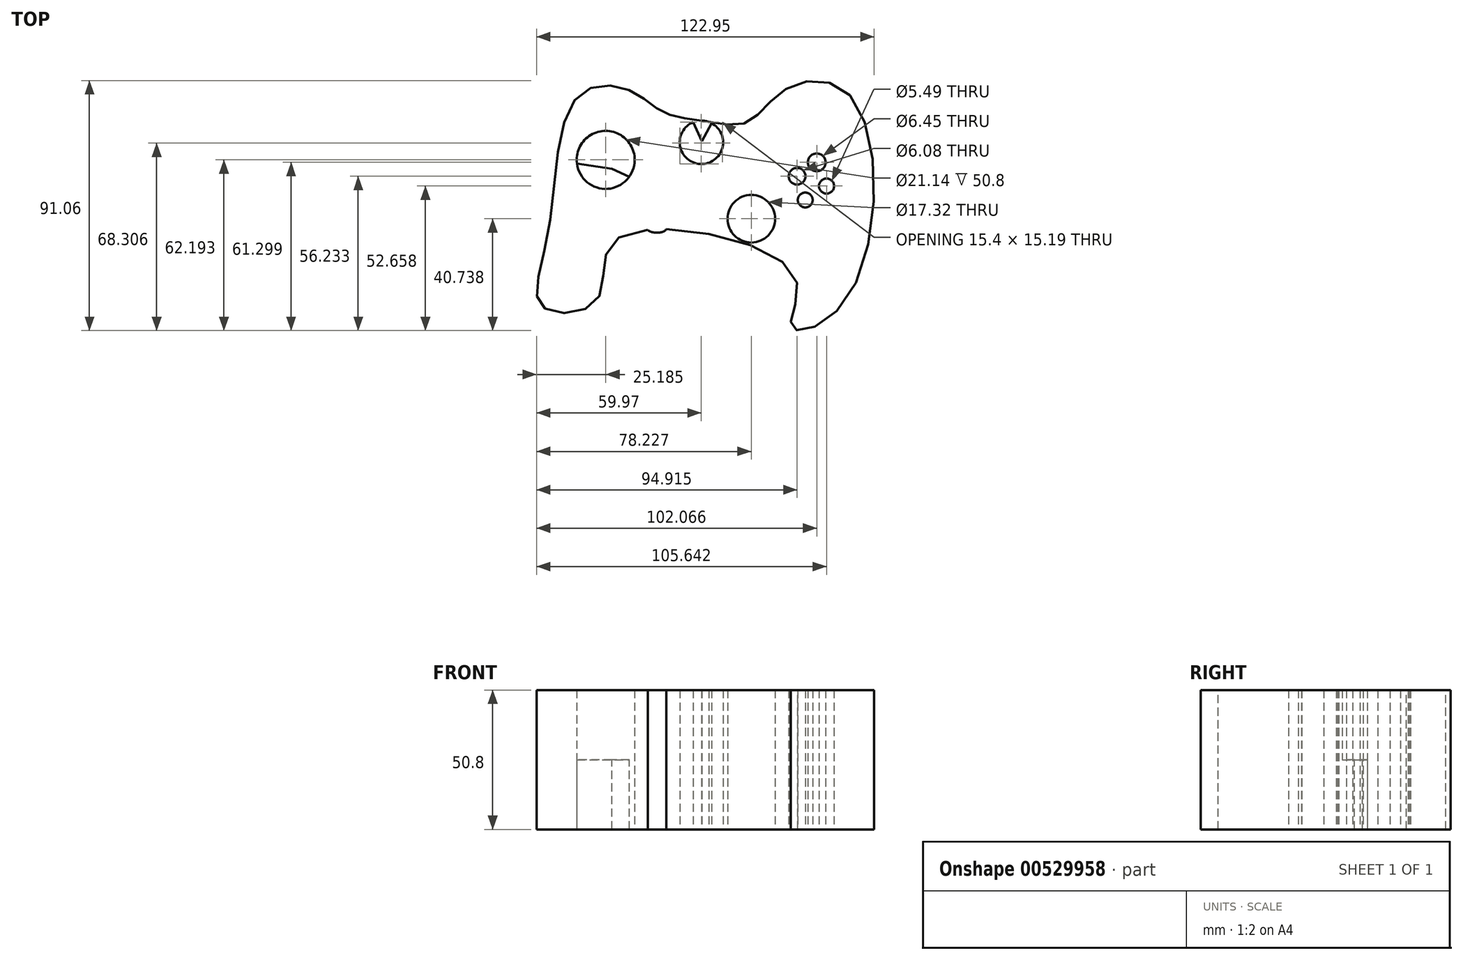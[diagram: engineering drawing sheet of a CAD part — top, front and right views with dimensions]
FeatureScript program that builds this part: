
annotation { "Feature Type Name" : "Feature", "Feature Type Description" : "" }
export const myFeature = defineFeature(function(context is Context, id is Id, definition is map)
    precondition{}
    {
        {
            var Q0;
            Q0=qCreatedBy(makeId("Top.planeOp"),FACE);
            var sketch = newSketch(context, id + "F0", { "sketchPlane" : qUnion([Q0])});
            skFitSpline(sketch, "E0", {"points": [v(-56.02, -34.12) * mm, v(-45.3, 16.54) * mm, v(-25.93, 18.92) * mm, v(-13.7, 10.88) * mm, v(0, 7.9) * mm, v(16.69, 7.3) * mm, v(30.4, 19.22) * mm, v(54.83, 16.24) * mm, v(52.15, -58.26) * mm, v(32.78, -67.2) * mm, v(33.67, -48.13) * mm, v(-31, -35.31) * mm, v(-38.14, -57.66) * mm, v(-57.8, -60.04) * mm, v(-56.02, -34.12) * mm]});
            skCircle(sketch, "E1", {"center": v(18.18, -27.86) * mm, "radius": 8.66 * mm});
            skCircle(sketch, "E2", {"center": v(-34.86, -6.4) * mm, "radius": 10.57 * mm});
            skCircle(sketch, "E3", {"center": v(34.86, -12.37) * mm, "radius": 3.04 * mm});
            skCircle(sketch, "E4", {"center": v(42.02, -7.3) * mm, "radius": 3.22 * mm});
            skCircle(sketch, "E5", {"center": v(45.6, -15.94) * mm, "radius": 2.75 * mm});
            skCircle(sketch, "E6", {"center": v(37.84, -21) * mm, "radius": 2.7 * mm});
            skCircle(sketch, "E7", {"center": v(0, 0) * mm, "radius": 7.9 * mm});
            skLineSegment(sketch, "E8", {"start": v(-3, 7.3) * mm, "end": v(3.68, -6.99) * mm});
            skLineSegment(sketch, "E9", {"start": v(3.68, 6.99) * mm, "end": v(-3.68, -6.99) * mm});
            skFitSpline(sketch, "E10", {"points": [v(-20.56, -23.1) * mm, v(-31.59, -22.5) * mm, v(-31, -26.37) * mm, v(-20.56, -27.56) * mm, v(-19.56, -31.9) * mm, v(-12.85, -31.67) * mm, v(-13.4, -27.56) * mm, v(-6.56, -27.56) * mm, v(-6.26, -22.5) * mm, v(-13.4, -22.2) * mm, v(-13.7, -15.35) * mm, v(-23.54, -14.45) * mm, v(-20.56, -23.1) * mm]});
            skSolve(sketch);
        }
        {
            var Q0;
            {var subQ0=sQuery(id+"F0.wireOp",EDGE,"E7");var subQ1=sQuery(id+"F0.wireOp",EDGE,"E0");var subQ2=makeQuery(id+"F0.imprint","INTERSECT",VERTEX,{"disambiguationData":[OD(0.0)],"derivedFrom":[subQ1,subQ0]});Q0=makeQuery(id+"F0.imprint","IMPRINT",FACE,{"disambiguationData":[TD([[makeQuery(id+"F0.imprint","IMPRINT",EDGE,{"disambiguationData":[TD([[subQ2,1.0]])],"derivedFrom":subQ1}),1.0]])]});}
            var Q1;
            {var subQ0=sQuery(id+"F0.wireOp",EDGE,"E10");var subQ1=sQuery(id+"F0.wireOp",EDGE,"E0");var subQ2=makeQuery(id+"F0.imprint","INTERSECT",VERTEX,{"disambiguationData":[OD(0.0)],"derivedFrom":[subQ1,subQ0]});Q1=makeQuery(id+"F0.imprint","IMPRINT",FACE,{"disambiguationData":[TD([[makeQuery(id+"F0.imprint","IMPRINT",EDGE,{"disambiguationData":[TD([[subQ2,-1.0]])],"derivedFrom":subQ1}),1.0]])]});}
            var Q2;
            {var subQ0=sQuery(id+"F0.wireOp",EDGE,"E10");var subQ1=sQuery(id+"F0.wireOp",EDGE,"E0");var subQ2=makeQuery(id+"F0.imprint","INTERSECT",VERTEX,{"disambiguationData":[OD(0.0)],"derivedFrom":[subQ1,subQ0]});Q2=makeQuery(id+"F0.imprint","IMPRINT",FACE,{"disambiguationData":[TD([[makeQuery(id+"F0.imprint","IMPRINT",EDGE,{"disambiguationData":[TD([[subQ2,-1.0]])],"derivedFrom":subQ1}),-1.0]])]});}
            var Q3;
            {var subQ1=sQuery(id+"F0.wireOp",EDGE,"E7");var subQ5=sQuery(id+"F0.wireOp",EDGE,"E0");var subQ8=makeQuery(id+"F0.imprint","INTERSECT",VERTEX,{"disambiguationData":[OD(0.0)],"derivedFrom":[subQ5,subQ1]});Q3=makeQuery(id+"F0.imprint","IMPRINT",FACE,{"disambiguationData":[TD([[makeQuery(id+"F0.imprint","IMPRINT",EDGE,{"disambiguationData":[TD([[subQ8,1.0]])],"derivedFrom":subQ5}),-1.0]])]});}
            var Q4;
            Q4=makeQuery(id+"F0.imprint","IMPRINT",FACE,{"disambiguationData":[TD([[makeQuery(id+"F0.imprint","IMPRINT",EDGE,{"derivedFrom":sQuery(id+"F0.wireOp",EDGE,"E1")}),-1.0]])]});
            extrude(context, id + "F1", {"entities" : qUnion([Q0, Q1, Q2, Q3, Q4]), "depth" : 25.4 * mm, "offsetDistance" : 25.4 * mm});
        }
        {
            var Q0;
            Q0=makeQuery(id+"F1.opExtrude","CAP_FACE",FACE,{"disambiguationData":[OSD([sQuery(id+"F0.wireOp",EDGE,"E0"),sQuery(id+"F0.wireOp",EDGE,"E1"),sQuery(id+"F0.wireOp",EDGE,"E2"),sQuery(id+"F0.wireOp",EDGE,"E3"),sQuery(id+"F0.wireOp",EDGE,"E4"),sQuery(id+"F0.wireOp",EDGE,"E5"),sQuery(id+"F0.wireOp",EDGE,"E6"),sQuery(id+"F0.wireOp",EDGE,"E7"),sQuery(id+"F0.wireOp",EDGE,"E8"),sQuery(id+"F0.wireOp",EDGE,"E9"),sQuery(id+"F0.wireOp",EDGE,"E10")])],"isStart":true});
            var sketch = newSketch(context, id + "F2", { "sketchPlane" : qUnion([Q0])});
            skCircle(sketch, "E11.cCircle", {"center": v(-46.78, 57.02) * mm, "radius": 48.94 * mm, "construction": true});
            skLineSegment(sketch, "E11.0", {"start": v(-0.83, 38.6) * mm, "end": v(-8.3, 25.88) * mm});
            skLineSegment(sketch, "E11.1", {"start": v(-8.3, 25.88) * mm, "end": v(-19.2, 15.92) * mm});
            skLineSegment(sketch, "E11.2", {"start": v(-19.2, 15.92) * mm, "end": v(-32.53, 9.62) * mm});
            skLineSegment(sketch, "E11.3", {"start": v(-32.53, 9.62) * mm, "end": v(-47.14, 7.52) * mm});
            skLineSegment(sketch, "E11.4", {"start": v(-47.14, 7.52) * mm, "end": v(-61.7, 9.83) * mm});
            skLineSegment(sketch, "E11.5", {"start": v(-61.7, 9.83) * mm, "end": v(-74.96, 16.32) * mm});
            skLineSegment(sketch, "E11.6", {"start": v(-74.96, 16.32) * mm, "end": v(-85.7, 26.44) * mm});
            skLineSegment(sketch, "E11.7", {"start": v(-85.7, 26.44) * mm, "end": v(-92.98, 39.27) * mm});
            skLineSegment(sketch, "E11.8", {"start": v(-92.98, 39.27) * mm, "end": v(-96.16, 53.68) * mm});
            skLineSegment(sketch, "E11.9", {"start": v(-96.16, 53.68) * mm, "end": v(-94.95, 68.38) * mm});
            skLineSegment(sketch, "E11.10", {"start": v(-94.95, 68.38) * mm, "end": v(-89.47, 82.08) * mm});
            skLineSegment(sketch, "E11.11", {"start": v(-89.47, 82.08) * mm, "end": v(-80.18, 93.54) * mm});
            skLineSegment(sketch, "E11.12", {"start": v(-80.18, 93.54) * mm, "end": v(-67.93, 101.77) * mm});
            skLineSegment(sketch, "E11.13", {"start": v(-67.93, 101.77) * mm, "end": v(-53.8, 106.02) * mm});
            skLineSegment(sketch, "E11.14", {"start": v(-53.8, 106.02) * mm, "end": v(-39.05, 105.9) * mm});
            skLineSegment(sketch, "E11.15", {"start": v(-39.05, 105.9) * mm, "end": v(-24.98, 101.46) * mm});
            skLineSegment(sketch, "E11.16", {"start": v(-24.98, 101.46) * mm, "end": v(-12.85, 93.06) * mm});
            skLineSegment(sketch, "E11.17", {"start": v(-12.85, 93.06) * mm, "end": v(-3.74, 81.46) * mm});
            skLineSegment(sketch, "E11.18", {"start": v(-3.74, 81.46) * mm, "end": v(1.56, 67.68) * mm});
            skLineSegment(sketch, "E11.19", {"start": v(1.56, 67.68) * mm, "end": v(2.55, 52.96) * mm});
            skLineSegment(sketch, "E11.20", {"start": v(2.55, 52.96) * mm, "end": v(-0.83, 38.6) * mm});
            skPoint(sketch, "E11.0.midPoint", {"position": v(-4.57, 32.24) * mm});
            skSolve(sketch);
        }
        {
            var Q0;
            {var subQ1=sQuery(id+"F2.wireOp",EDGE,"E11.1");Q0=makeQuery(id+"F2.imprint","IMPRINT",FACE,{"disambiguationData":[TD([[makeQuery(id+"F2.imprint","IMPRINT",EDGE,{"derivedFrom":subQ1}),-1.0]])]});}
            var Q1;
            {var subQ0=sQuery(id+"F2.wireOp",EDGE,"E11.3");var subQ1=sQuery(id+"F2.wireOp",EDGE,"E11.2");var subQ2=makeQuery(id+"F2.imprint","INTERSECT",VERTEX,{"derivedFrom":[subQ1,subQ0]});Q1=makeQuery(id+"F2.imprint","IMPRINT",FACE,{"disambiguationData":[TD([[makeQuery(id+"F2.imprint","IMPRINT",EDGE,{"disambiguationData":[TD([[subQ2,1.0]])],"derivedFrom":subQ1}),-1.0]])]});}
            extrude(context, id + "F3", {"entities" : qUnion([Q0, Q1]), "operationType" : NewBodyOperationType.ADD, "depth" : 25.4 * mm, "offsetDistance" : 25.4 * mm});
        }
        {
            var Q0;
            Q0=makeQuery(id+"F1.opExtrude","CAP_FACE",FACE,{"disambiguationData":[OSD([sQuery(id+"F0.wireOp",EDGE,"E0"),sQuery(id+"F0.wireOp",EDGE,"E1"),sQuery(id+"F0.wireOp",EDGE,"E2"),sQuery(id+"F0.wireOp",EDGE,"E3"),sQuery(id+"F0.wireOp",EDGE,"E4"),sQuery(id+"F0.wireOp",EDGE,"E5"),sQuery(id+"F0.wireOp",EDGE,"E6"),sQuery(id+"F0.wireOp",EDGE,"E7"),sQuery(id+"F0.wireOp",EDGE,"E8"),sQuery(id+"F0.wireOp",EDGE,"E9"),sQuery(id+"F0.wireOp",EDGE,"E10")])],"isStart":true});
            extrude(context, id + "F4", {"entities" : qUnion([Q0]), "operationType" : NewBodyOperationType.ADD, "depth" : 25.4 * mm, "offsetDistance" : 25.4 * mm});
        }
    });
